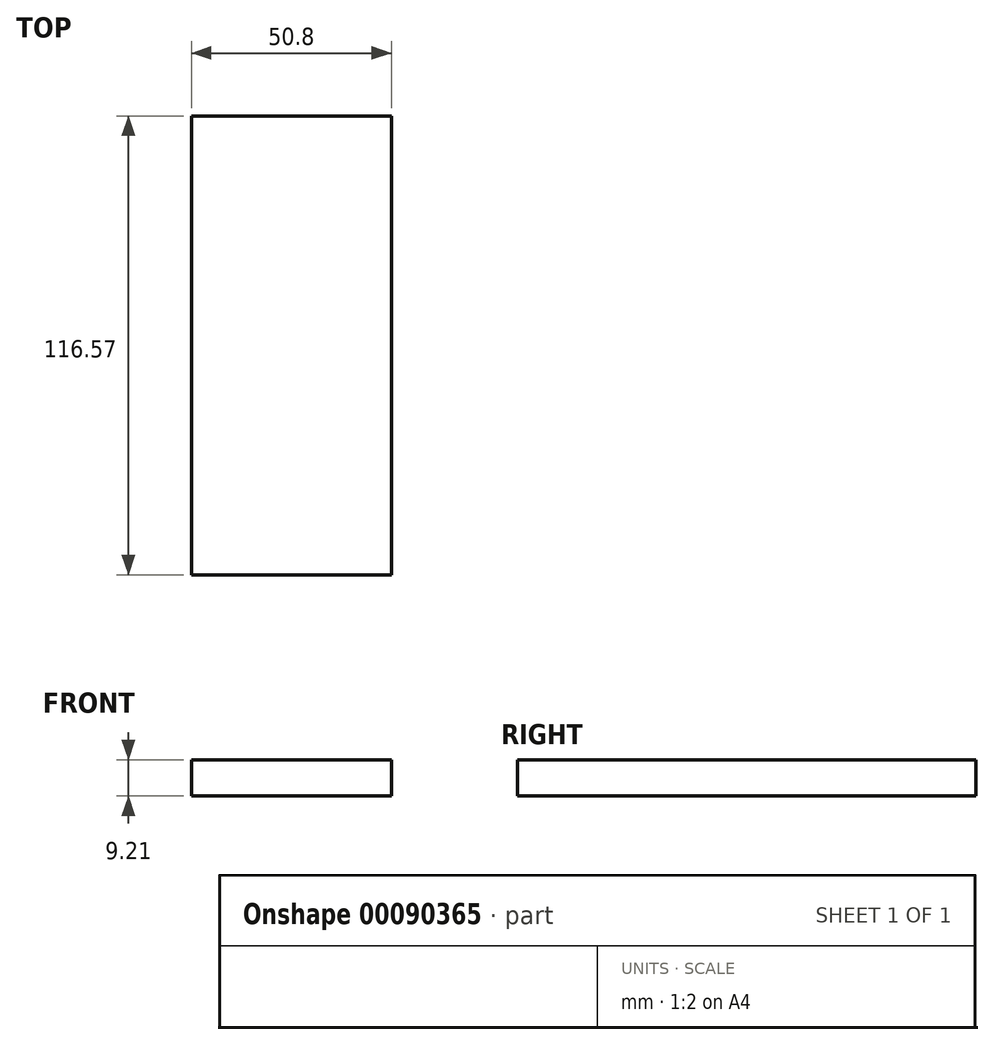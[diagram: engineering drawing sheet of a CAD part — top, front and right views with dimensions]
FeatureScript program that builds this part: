
annotation { "Feature Type Name" : "Feature", "Feature Type Description" : "" }
export const myFeature = defineFeature(function(context is Context, id is Id, definition is map)
    precondition{}
    {
        {
            var Q0;
            Q0=qCreatedBy(makeId("Right.planeOp"),FACE);
            var sketch = newSketch(context, id + "F0", { "sketchPlane" : qUnion([Q0])});
            skLineSegment(sketch, "E0.bottom", {"start": v(107.13, -37.36) * mm, "end": v(-9.44, -37.36) * mm});
            skLineSegment(sketch, "E0.top", {"start": v(107.13, -46.57) * mm, "end": v(-9.44, -46.57) * mm});
            skLineSegment(sketch, "E0.left", {"start": v(107.13, -37.36) * mm, "end": v(107.13, -46.57) * mm});
            skLineSegment(sketch, "E0.right", {"start": v(-9.44, -37.36) * mm, "end": v(-9.44, -46.57) * mm});
            skSolve(sketch);
        }
        {
            var Q0;
            Q0=makeQuery(id+"F0.imprint","IMPRINT",FACE,{"disambiguationData":[TD([[makeQuery(id+"F0.imprint","IMPRINT",EDGE,{"derivedFrom":sQuery(id+"F0.wireOp",EDGE,"E0.bottom")}),1.0]])]});
            extrude(context, id + "F1", {"entities" : qUnion([Q0]), "depth" : 25.4 * mm, "hasSecondDirection" : true, "secondDirectionOppositeDirection" : true, "secondDirectionDepth" : 25.4 * mm});
        }
    });
